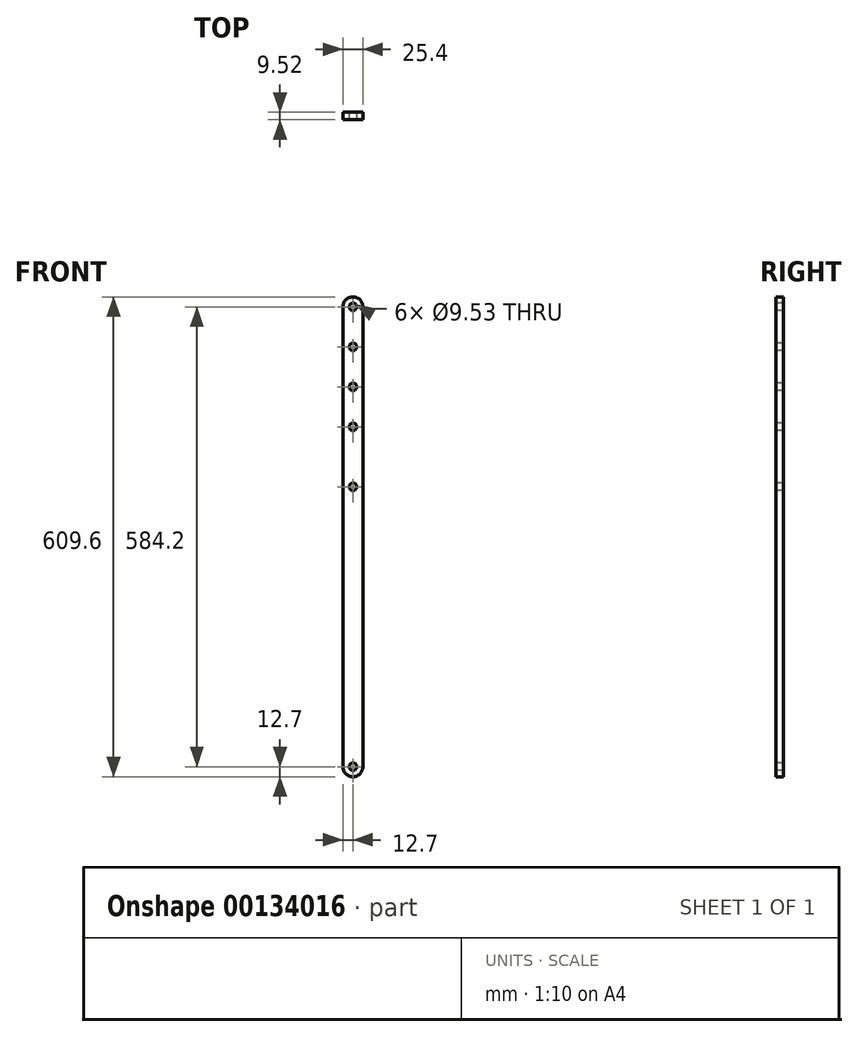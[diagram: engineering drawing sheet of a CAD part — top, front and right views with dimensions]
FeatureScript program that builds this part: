
annotation { "Feature Type Name" : "Feature", "Feature Type Description" : "" }
export const myFeature = defineFeature(function(context is Context, id is Id, definition is map)
    precondition{}
    {
        {
            var Q0;
            Q0=qCreatedBy(makeId("Front.planeOp"),FACE);
            var sketch = newSketch(context, id + "F0", { "sketchPlane" : qUnion([Q0])});
            skLineSegment(sketch, "E0.bottom", {"start": v(-12.7, 304.8) * mm, "end": v(12.7, 304.8) * mm});
            skLineSegment(sketch, "E0.top", {"start": v(-12.7, -304.8) * mm, "end": v(12.7, -304.8) * mm});
            skLineSegment(sketch, "E0.left", {"start": v(-12.7, 304.8) * mm, "end": v(-12.7, -304.8) * mm});
            skLineSegment(sketch, "E0.right", {"start": v(12.7, 304.8) * mm, "end": v(12.7, -304.8) * mm});
            skLineSegment(sketch, "E1", {"start": v(0, 304.8) * mm, "end": v(0, -304.8) * mm, "construction": true});
            skSolve(sketch);
        }
        {
            var Q0;
            Q0 = qSketchRegion(id + "F0", true);
            extrude(context, id + "F1", {"entities" : qUnion([Q0]), "endBound" : BoundingType.SYMMETRIC, "depth" : 9.52 * mm});
        }
        {
            var Q0;
            Q0=makeQuery(id+"F1.opExtrude","SWEPT_EDGE",EDGE,{"disambiguationData":[OSD([sQuery(id+"F0.wireOp",EDGE,"E0.bottom"),sQuery(id+"F0.wireOp",EDGE,"E0.right")])]});
            var Q1;
            Q1=makeQuery(id+"F1.opExtrude","SWEPT_EDGE",EDGE,{"disambiguationData":[OSD([sQuery(id+"F0.wireOp",EDGE,"E0.bottom"),sQuery(id+"F0.wireOp",EDGE,"E0.left")])]});
            var Q2;
            Q2=makeQuery(id+"F1.opExtrude","SWEPT_EDGE",EDGE,{"disambiguationData":[OSD([sQuery(id+"F0.wireOp",EDGE,"E0.top"),sQuery(id+"F0.wireOp",EDGE,"E0.left")])]});
            var Q3;
            Q3=makeQuery(id+"F1.opExtrude","SWEPT_EDGE",EDGE,{"disambiguationData":[OSD([sQuery(id+"F0.wireOp",EDGE,"E0.top"),sQuery(id+"F0.wireOp",EDGE,"E0.right")])]});
            fillet(context, id + "F2", {"entities" : qUnion([Q0, Q1, Q2, Q3]), "radius" : 12.7 * mm, "tangentPropagation" : true, "allowEdgeOverflow" : false});
        }
        {
            var Q0;
            Q0=makeQuery(id+"F1.opExtrude","CAP_FACE",FACE,{"disambiguationData":[OSD([sQuery(id+"F0.wireOp",EDGE,"E0.bottom"),sQuery(id+"F0.wireOp",EDGE,"E0.top"),sQuery(id+"F0.wireOp",EDGE,"E0.left"),sQuery(id+"F0.wireOp",EDGE,"E0.right")])],"isStart":false});
            var sketch = newSketch(context, id + "F3", { "sketchPlane" : qUnion([Q0])});
            skPoint(sketch, "E2", {"position": v(0, -292.1) * mm});
            skLineSegment(sketch, "E3", {"start": v(0, -292.1) * mm, "end": v(0, 292.1) * mm, "construction": true});
            skPoint(sketch, "E4", {"position": v(0, 63.5) * mm});
            skPoint(sketch, "E5", {"position": v(0, 241.3) * mm});
            skPoint(sketch, "E6", {"position": v(0, 190.5) * mm});
            skPoint(sketch, "E7", {"position": v(0, 139.7) * mm});
            skSolve(sketch);
        }
        {
            var Q0;
            Q0=sQuery(id+"F3.wireOp",VERTEX,"E2");
            var Q1;
            Q1=sQuery(id+"F3.wireOp",VERTEX,"E3.end");
            var Q2;
            Q2=sQuery(id+"F3.wireOp",VERTEX,"E4");
            var Q3;
            Q3=sQuery(id+"F3.wireOp",VERTEX,"E5");
            var Q4;
            Q4=sQuery(id+"F3.wireOp",VERTEX,"E6");
            var Q5;
            Q5=sQuery(id+"F3.wireOp",VERTEX,"E7");
            var Q6;
            Q6=makeQuery(id+"F1.opExtrude","SWEPT_BODY",BODY,{"disambiguationData":[OSD([sQuery(id+"F0.wireOp",EDGE,"E0.bottom"),sQuery(id+"F0.wireOp",EDGE,"E0.top"),sQuery(id+"F0.wireOp",EDGE,"E0.left"),sQuery(id+"F0.wireOp",EDGE,"E0.right")])]});
            hole(context, id + "F4", {"style" : HoleStyle.SIMPLE, "endStyle" : HoleEndStyle.THROUGH, "holeDiameter" : 9.52 * mm, "locations" : qUnion([Q0, Q1, Q2, Q3, Q4, Q5]), "scope" : qUnion([Q6]), "isTappedThrough" : true});
        }
    });
